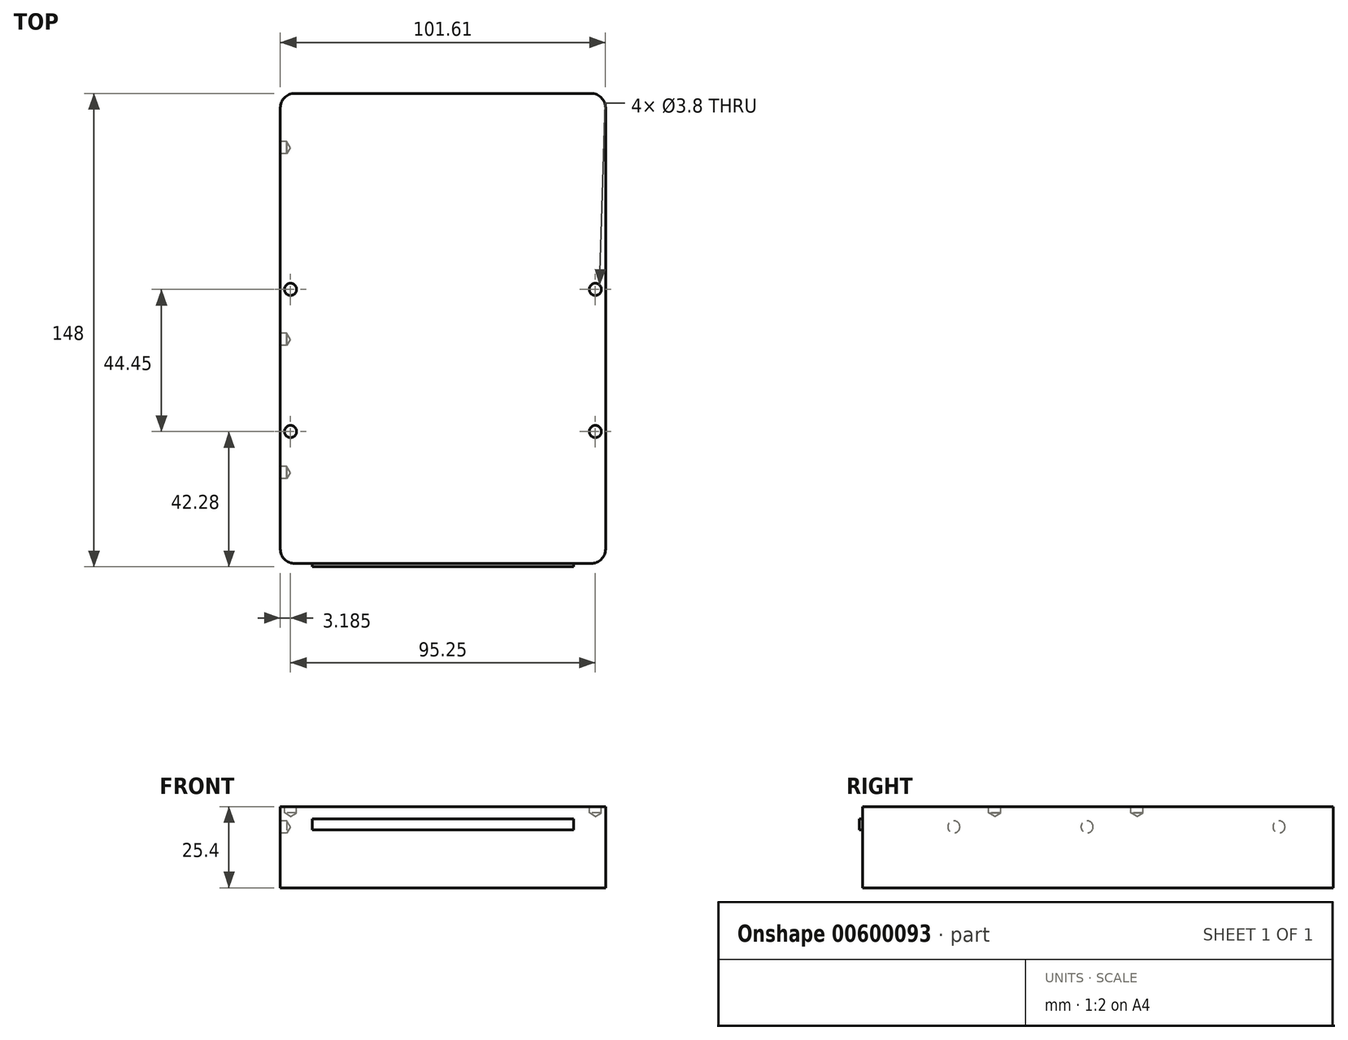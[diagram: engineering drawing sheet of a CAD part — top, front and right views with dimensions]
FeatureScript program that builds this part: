
annotation { "Feature Type Name" : "Feature", "Feature Type Description" : "" }
export const myFeature = defineFeature(function(context is Context, id is Id, definition is map)
    precondition{}
    {
        {
            var Q0;
            Q0=qCreatedBy(makeId("Top.planeOp"),FACE);
            var sketch = newSketch(context, id + "F0", { "sketchPlane" : qUnion([Q0])});
            skLineSegment(sketch, "E0.bottom", {"start": v(50.8, 73.5) * mm, "end": v(-50.8, 73.5) * mm});
            skLineSegment(sketch, "E0.top", {"start": v(50.8, -73.5) * mm, "end": v(-50.8, -73.5) * mm});
            skLineSegment(sketch, "E0.left", {"start": v(50.8, 73.5) * mm, "end": v(50.8, -73.5) * mm});
            skLineSegment(sketch, "E0.right", {"start": v(-50.8, 73.5) * mm, "end": v(-50.8, -73.5) * mm});
            skPoint(sketch, "E0.middle", {"position": v(0, 0) * mm});
            skPoint(sketch, "E1", {"position": v(-47.63, 12.23) * mm});
            skPoint(sketch, "E2", {"position": v(-47.63, -32.22) * mm});
            skPoint(sketch, "E3", {"position": v(47.62, -32.22) * mm});
            skPoint(sketch, "E4", {"position": v(47.62, 12.23) * mm});
            skSolve(sketch);
        }
        {
            var Q0;
            Q0=makeQuery(id+"F0.imprint","IMPRINT",FACE,{"disambiguationData":[TD([[makeQuery(id+"F0.imprint","IMPRINT",EDGE,{"derivedFrom":sQuery(id+"F0.wireOp",EDGE,"E0.bottom")}),1.0]])]});
            extrude(context, id + "F1", {"entities" : qUnion([Q0]), "oppositeDirection" : true, "depth" : 25.4 * mm, "offsetDistance" : 25 * mm});
        }
        {
            var Q0;
            Q0=sQuery(id+"F0.wireOp",VERTEX,"E3");
            var Q1;
            Q1=sQuery(id+"F0.wireOp",VERTEX,"E2");
            var Q2;
            Q2=sQuery(id+"F0.wireOp",VERTEX,"E1");
            var Q3;
            Q3=sQuery(id+"F0.wireOp",VERTEX,"E4");
            var Q4;
            Q4=makeQuery(id+"F1.opExtrude","SWEPT_BODY",BODY,{"disambiguationData":[OSD([sQuery(id+"F0.wireOp",EDGE,"E0.bottom"),sQuery(id+"F0.wireOp",EDGE,"E0.top"),sQuery(id+"F0.wireOp",EDGE,"E0.left"),sQuery(id+"F0.wireOp",EDGE,"E0.right")])]});
            hole(context, id + "F2", {"style" : HoleStyle.SIMPLE, "endStyle" : HoleEndStyle.BLIND, "standardTappedOrClearance" : lookupTablePath({ "standard" : "ANSI", "fit" : "Normal (ASME)", "size" : "#6", "type" : "Clearance" }), "standardBlindInLast" : lookupTablePath({ "fit" : "Free", "standard" : "ANSI", "size" : "#6", "type" : "Clearance" }), "holeDiameter" : 3.8 * mm, "majorDiameter" : 5 * mm, "holeDepth" : 2 * mm, "isTappedThrough" : true, "tappedDepth" : 12 * mm, "tapClearance" : 3, "locations" : qUnion([Q0, Q1, Q2, Q3]), "scope" : qUnion([Q4])});
        }
        {
            var Q0;
            Q0=makeQuery(id+"F1.opExtrude","SWEPT_EDGE",EDGE,{"disambiguationData":[OSD([sQuery(id+"F0.wireOp",EDGE,"E0.bottom"),sQuery(id+"F0.wireOp",EDGE,"E0.left")])]});
            var Q1;
            Q1=makeQuery(id+"F1.opExtrude","SWEPT_EDGE",EDGE,{"disambiguationData":[OSD([sQuery(id+"F0.wireOp",EDGE,"E0.bottom"),sQuery(id+"F0.wireOp",EDGE,"E0.right")])]});
            var Q2;
            Q2=makeQuery(id+"F1.opExtrude","SWEPT_EDGE",EDGE,{"disambiguationData":[OSD([sQuery(id+"F0.wireOp",EDGE,"E0.top"),sQuery(id+"F0.wireOp",EDGE,"E0.right")])]});
            var Q3;
            Q3=makeQuery(id+"F1.opExtrude","SWEPT_EDGE",EDGE,{"disambiguationData":[OSD([sQuery(id+"F0.wireOp",EDGE,"E0.top"),sQuery(id+"F0.wireOp",EDGE,"E0.left")])]});
            fillet(context, id + "F3", {"entities" : qUnion([Q0, Q1, Q2, Q3]), "radius" : 4.5 * mm, "tangentPropagation" : true, "allowEdgeOverflow" : false});
        }
        {
            var Q0;
            Q0=makeQuery(id+"F1.opExtrude","SWEPT_FACE",FACE,{"disambiguationData":[OSD([sQuery(id+"F0.wireOp",EDGE,"E0.right")])]});
            var sketch = newSketch(context, id + "F4", { "sketchPlane" : qUnion([Q0])});
            skPoint(sketch, "E5", {"position": v(45, -6.36) * mm});
            skPoint(sketch, "E6", {"position": v(3.39, -6.36) * mm});
            skPoint(sketch, "E7", {"position": v(-56.6, -6.36) * mm});
            skSolve(sketch);
        }
        {
            var Q0;
            Q0=sQuery(id+"F4.wireOp",VERTEX,"E5");
            var Q1;
            Q1=sQuery(id+"F4.wireOp",VERTEX,"E6");
            var Q2;
            Q2=sQuery(id+"F4.wireOp",VERTEX,"E7");
            var Q3;
            Q3=makeQuery(id+"F1.opExtrude","SWEPT_BODY",BODY,{"disambiguationData":[OSD([sQuery(id+"F0.wireOp",EDGE,"E0.bottom"),sQuery(id+"F0.wireOp",EDGE,"E0.top"),sQuery(id+"F0.wireOp",EDGE,"E0.left"),sQuery(id+"F0.wireOp",EDGE,"E0.right")])]});
            hole(context, id + "F5", {"style" : HoleStyle.SIMPLE, "endStyle" : HoleEndStyle.BLIND, "standardTappedOrClearance" : lookupTablePath({ "standard" : "ANSI", "fit" : "Normal (ASME)", "size" : "#6", "type" : "Clearance" }), "standardBlindInLast" : lookupTablePath({ "fit" : "Free", "standard" : "ANSI", "size" : "#6", "type" : "Clearance" }), "holeDiameter" : 3.8 * mm, "majorDiameter" : 5 * mm, "holeDepth" : 2 * mm, "isTappedThrough" : true, "tappedDepth" : 12 * mm, "tapClearance" : 3, "locations" : qUnion([Q0, Q1, Q2]), "scope" : qUnion([Q3])});
        }
        {
            var Q0;
            Q0=makeQuery(id+"F1.opExtrude","SWEPT_FACE",FACE,{"disambiguationData":[OSD([sQuery(id+"F0.wireOp",EDGE,"E0.top")])]});
            var sketch = newSketch(context, id + "F6", { "sketchPlane" : qUnion([Q0])});
            skPoint(sketch, "E8", {"position": v(0, -5.57) * mm});
            skLineSegment(sketch, "E9.bottom", {"start": v(-40.86, -3.9) * mm, "end": v(40.86, -3.9) * mm});
            skLineSegment(sketch, "E9.top", {"start": v(-40.86, -7.24) * mm, "end": v(40.86, -7.24) * mm});
            skLineSegment(sketch, "E9.left", {"start": v(-40.86, -3.9) * mm, "end": v(-40.86, -7.24) * mm});
            skLineSegment(sketch, "E9.right", {"start": v(40.86, -3.9) * mm, "end": v(40.86, -7.24) * mm});
            skSolve(sketch);
        }
        {
            var Q0;
            Q0=makeQuery(id+"F6.imprint","IMPRINT",FACE,{"disambiguationData":[TD([[makeQuery(id+"F6.imprint","IMPRINT",EDGE,{"derivedFrom":sQuery(id+"F6.wireOp",EDGE,"E9.bottom")}),-1.0]])]});
            extrude(context, id + "F7", {"entities" : qUnion([Q0]), "operationType" : NewBodyOperationType.ADD, "depth" : 1 * mm, "offsetDistance" : 25 * mm});
        }
    });
